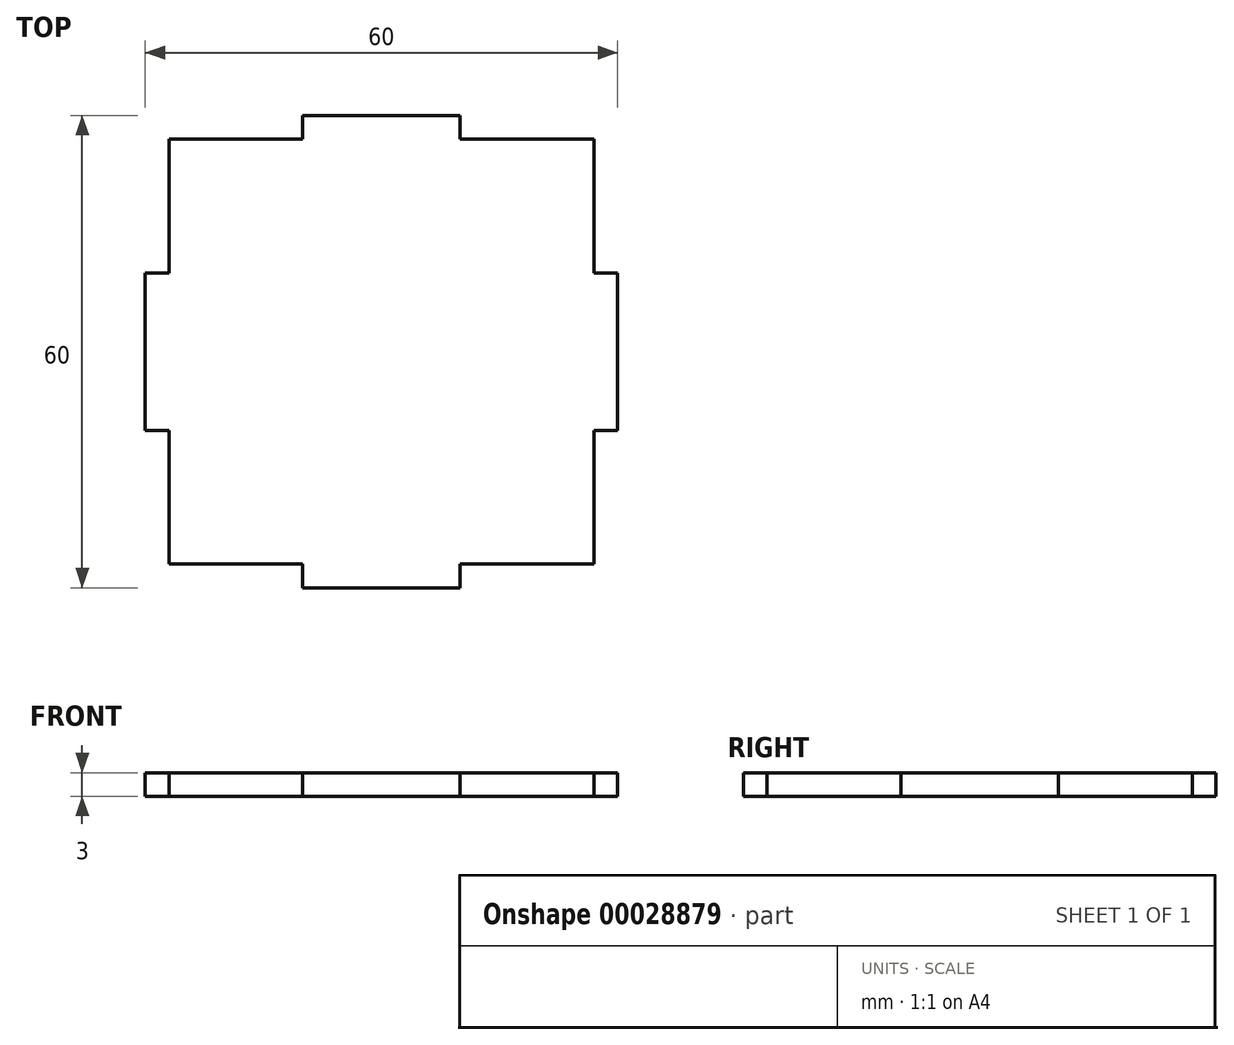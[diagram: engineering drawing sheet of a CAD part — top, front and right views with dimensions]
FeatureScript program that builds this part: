
annotation { "Feature Type Name" : "Feature", "Feature Type Description" : "" }
export const myFeature = defineFeature(function(context is Context, id is Id, definition is map)
    precondition{}
    {
        {
            var Q0;
            Q0=qCreatedBy(makeId("Top.planeOp"),FACE);
            var sketch = newSketch(context, id + "F0", { "sketchPlane" : qUnion([Q0])});
            skLineSegment(sketch, "E0", {"start": v(0, 30) * mm, "end": v(-10, 30) * mm});
            skLineSegment(sketch, "E1", {"start": v(-10, 30) * mm, "end": v(-10, 27) * mm});
            skLineSegment(sketch, "E2", {"start": v(-10, 27) * mm, "end": v(-27, 27) * mm});
            skLineSegment(sketch, "E3", {"start": v(-27, 27) * mm, "end": v(-27, 10) * mm});
            skLineSegment(sketch, "E4", {"start": v(-27, 10) * mm, "end": v(-30, 10) * mm});
            skLineSegment(sketch, "E5", {"start": v(-30, 10) * mm, "end": v(-30, 0) * mm});
            skLineSegment(sketch, "E6.MirrorCS", {"start": v(10, 30) * mm, "end": v(10, 27) * mm});
            skLineSegment(sketch, "E7.MirrorCS", {"start": v(27, 10) * mm, "end": v(30, 10) * mm});
            skLineSegment(sketch, "E8.MirrorCS", {"start": v(0, 30) * mm, "end": v(10, 30) * mm});
            skLineSegment(sketch, "E9.MirrorCS", {"start": v(30, 10) * mm, "end": v(30, 0) * mm});
            skLineSegment(sketch, "E10.MirrorCS", {"start": v(27, 27) * mm, "end": v(27, 10) * mm});
            skLineSegment(sketch, "E11.MirrorCS", {"start": v(10, 27) * mm, "end": v(27, 27) * mm});
            skLineSegment(sketch, "E12.MirrorCS", {"start": v(27, -10) * mm, "end": v(30, -10) * mm});
            skLineSegment(sketch, "E13.MirrorCS", {"start": v(10, -30) * mm, "end": v(10, -27) * mm});
            skLineSegment(sketch, "E14.MirrorCS", {"start": v(-10, -30) * mm, "end": v(-10, -27) * mm});
            skLineSegment(sketch, "E15.MirrorCS", {"start": v(-27, -10) * mm, "end": v(-30, -10) * mm});
            skLineSegment(sketch, "E16.MirrorCS", {"start": v(10, -27) * mm, "end": v(27, -27) * mm});
            skLineSegment(sketch, "E17.MirrorCS", {"start": v(27, -27) * mm, "end": v(27, -10) * mm});
            skLineSegment(sketch, "E18.MirrorCS", {"start": v(30, -10) * mm, "end": v(30, 0) * mm});
            skLineSegment(sketch, "E19.MirrorCS", {"start": v(0, -30) * mm, "end": v(10, -30) * mm});
            skLineSegment(sketch, "E20.MirrorCS", {"start": v(-30, -10) * mm, "end": v(-30, 0) * mm});
            skLineSegment(sketch, "E21.MirrorCS", {"start": v(-10, -27) * mm, "end": v(-27, -27) * mm});
            skLineSegment(sketch, "E22.MirrorCS", {"start": v(0, -30) * mm, "end": v(-10, -30) * mm});
            skLineSegment(sketch, "E23.MirrorCS", {"start": v(-27, -27) * mm, "end": v(-27, -10) * mm});
            skSolve(sketch);
        }
        {
            var Q0;
            Q0=makeQuery(id+"F0.imprint","IMPRINT",FACE,{"disambiguationData":[TD([[makeQuery(id+"F0.imprint","IMPRINT",EDGE,{"derivedFrom":sQuery(id+"F0.wireOp",EDGE,"E0")}),1.0]])]});
            extrude(context, id + "F1", {"entities" : qUnion([Q0]), "depth" : 3 * mm});
        }
    });
